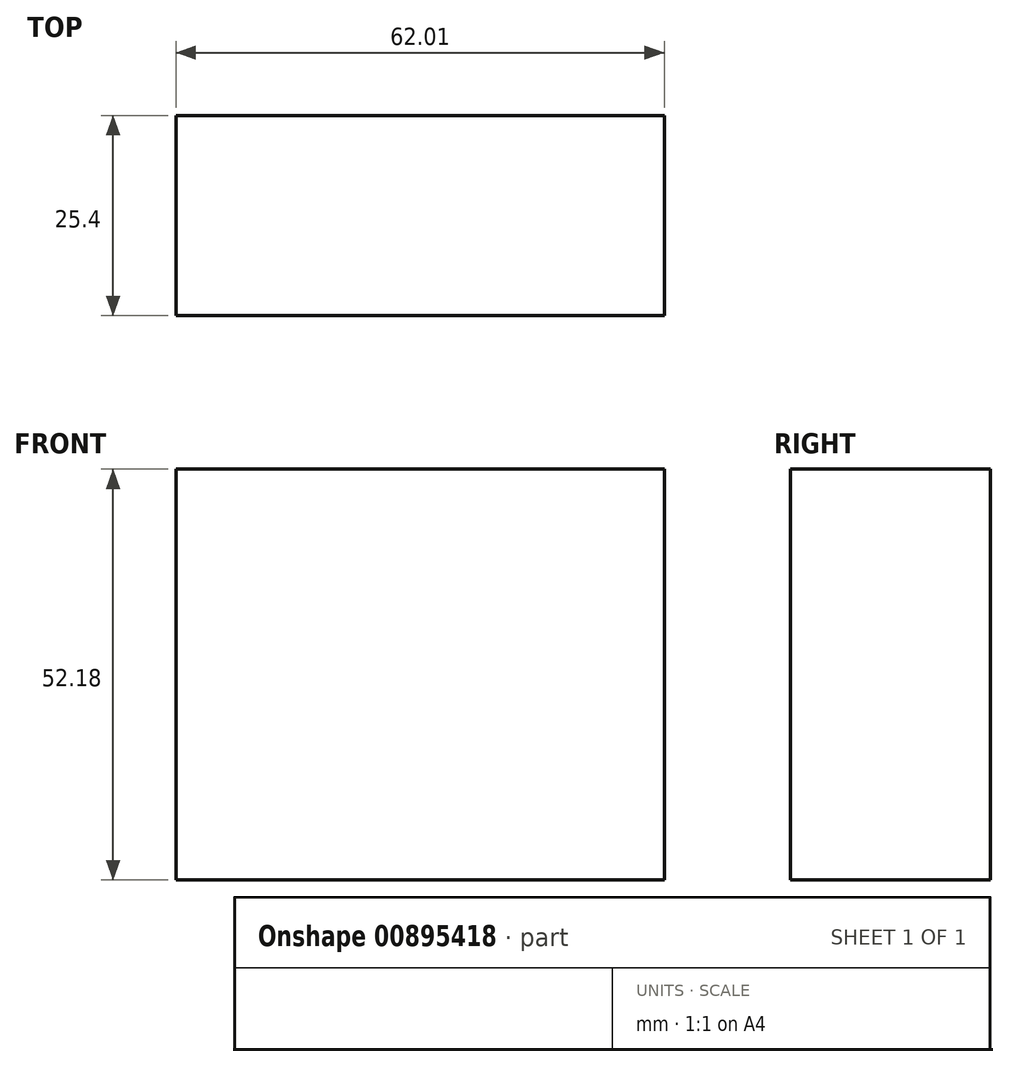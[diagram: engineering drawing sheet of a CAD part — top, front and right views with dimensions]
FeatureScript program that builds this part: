
annotation { "Feature Type Name" : "Feature", "Feature Type Description" : "" }
export const myFeature = defineFeature(function(context is Context, id is Id, definition is map)
    precondition{}
    {
        {
            var Q0;
            Q0=qCreatedBy(makeId("Front.planeOp"),FACE);
            var sketch = newSketch(context, id + "F0", { "sketchPlane" : qUnion([Q0])});
            skLineSegment(sketch, "E0.bottom", {"start": v(-36.5, -19.43) * mm, "end": v(25.52, -19.43) * mm});
            skLineSegment(sketch, "E0.top", {"start": v(-36.5, 32.75) * mm, "end": v(25.52, 32.75) * mm});
            skLineSegment(sketch, "E0.left", {"start": v(-36.5, -19.43) * mm, "end": v(-36.5, 32.75) * mm});
            skLineSegment(sketch, "E0.right", {"start": v(25.52, -19.43) * mm, "end": v(25.52, 32.75) * mm});
            skSolve(sketch);
        }
        {
            var Q0;
            Q0=makeQuery(id+"F0.imprint","IMPRINT",FACE,{"disambiguationData":[TD([[makeQuery(id+"F0.imprint","IMPRINT",EDGE,{"derivedFrom":sQuery(id+"F0.wireOp",EDGE,"E0.bottom")}),1.0]])]});
            extrude(context, id + "F1", {"entities" : qUnion([Q0]), "depth" : 25.4 * mm, "offsetDistance" : 25.4 * mm});
        }
    });
